# Revit family: Plumbing_Valves_Bermad_750-6E_Level_Control_Valve_with_Solenoid
name_source: partatom
category: Pipe Accessories
units: mm (PartAtom-declared; Revit-internal decimal feet)

## family parameters
Always vertical = Yes
Cut with Voids When Loaded = No
OmniClass Number = 23.65.55.14.17
OmniClass Title = Adjusting/Controlling Valves for Liquid Services
Part Type = Valve - Breaks Into
Round Connector Dimension = Use Diameter
Shared = No
Work Plane-Based = No

## types (4) — shared parameters
Act_Ang = 25.00°
Assembly Code = D2020300
Date of publishing = 30/05/2019
Description = Level Control Valve with Solenoid Control
Has External hydraulic Command = No
Indicator = No
Main Side Trim = 200 mm  [stored 0.656168 ft]
Manufacturer = BERMAD
Model = 750-6E
Model URL = https://www.bermad.com
Pilot_Alt = No
Pilot_Int = No
Pilot_PB = No
Solenoid Operated = Yes
Top Trim = 160 mm  [stored 0.524934 ft]
URL = WWW.BERMAD.COM
Use V Port = No
zero-valued in all types: K Coefficient, Secoundary Side Trim

## per-type parameters (varying)
| type | Basic Valve Series | Type Comments |
| Grooved (1.5"-8", DN40-DN200) | 700 Grooved | Sizes: 1.5", 2", 2.5", 3", 4", 6", 8" / DN40, DN50, DN65, DN80, DN100, DN150, DN200 |
| Flanged EN (1.5"-12", DN40-DN300) | EN Series | Sizes: 1.5", 2", 2.5", 3", 4", 6", 8", 10", 12" / DN40, DN50, DN65, DN80, DN100, DN150, DN200, DN250, DN300 |
| Flanged ES (2.5"-12", DN65-DN300) | ES Series | Sizes: 2.5", 3", 4", 6", 8", 10", 12" / DN65, DN80, DN100, DN150, DN200, DN250, DN300 |
| Threaded (1.5"-3", DN40-DN80) | 700 Threaded | Sizes: 1.5", 2", 2.5", 3" / DN40, DN50, DN65, DN80 |

note: [stored X ft] marks values corroborated as IEEE doubles in the binary element streams (Revit-internal decimal feet)

## geometry (parser evidence)
native form markers: Blend x2, Sweep x4
no freeform markers — native parametric forms only
